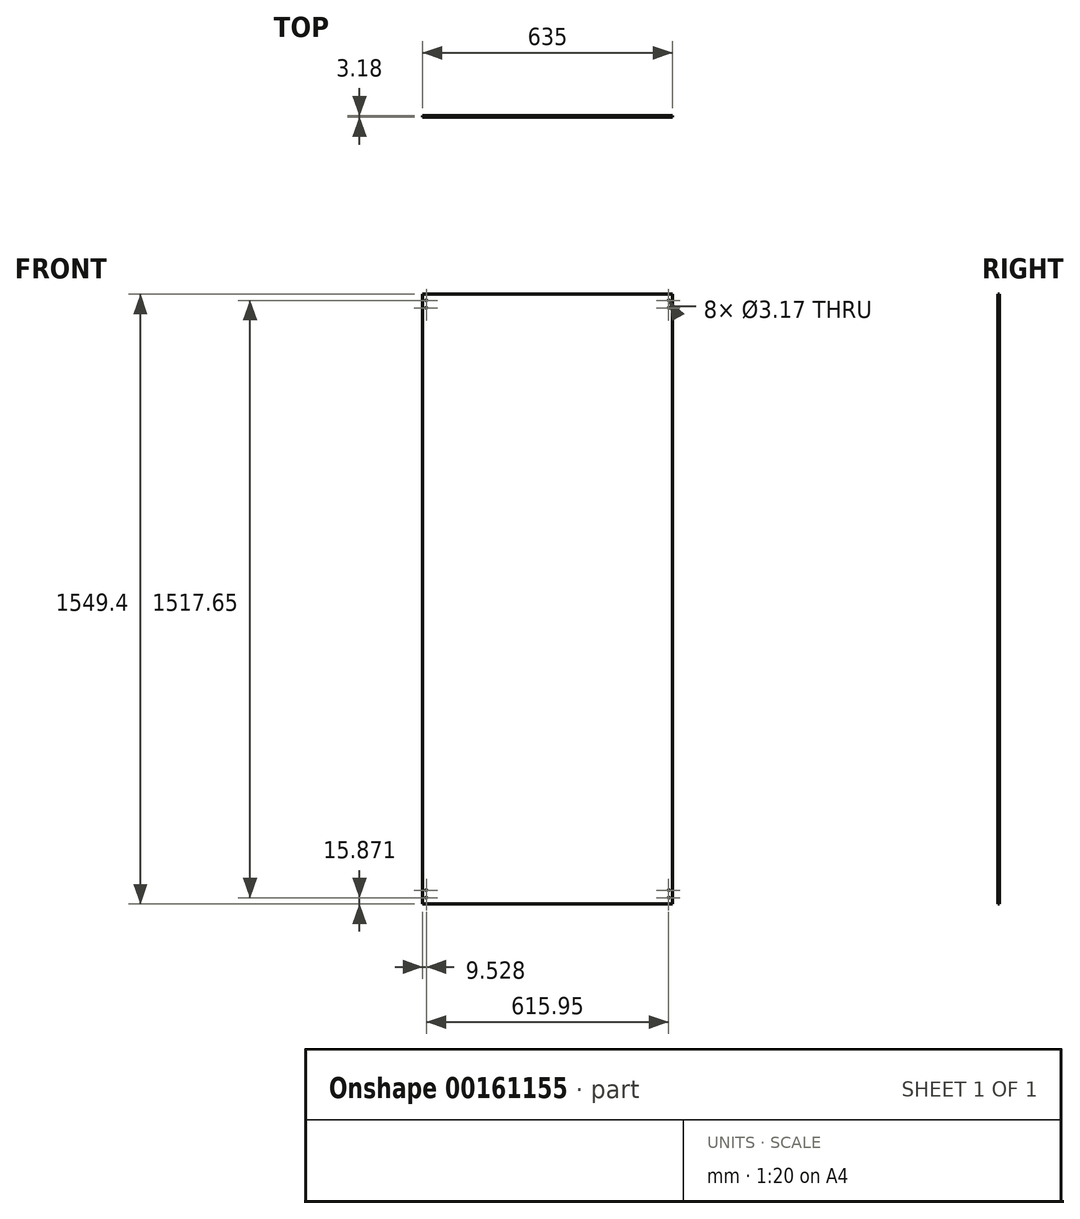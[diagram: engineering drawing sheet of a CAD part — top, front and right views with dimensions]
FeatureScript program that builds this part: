
annotation { "Feature Type Name" : "Feature", "Feature Type Description" : "" }
export const myFeature = defineFeature(function(context is Context, id is Id, definition is map)
    precondition{}
    {
        {
            var Q0;
            Q0=qCreatedBy(makeId("Front.planeOp"),FACE);
            var sketch = newSketch(context, id + "F0", { "sketchPlane" : qUnion([Q0])});
            skLineSegment(sketch, "E0.bottom", {"start": v(-379.1, 732.72) * mm, "end": v(255.9, 732.72) * mm});
            skLineSegment(sketch, "E0.left", {"start": v(-379.1, 732.72) * mm, "end": v(-379.1, -816.68) * mm});
            skLineSegment(sketch, "E0.right", {"start": v(255.9, 732.72) * mm, "end": v(255.9, -816.68) * mm});
            skLineSegment(sketch, "E1", {"start": v(255.9, -816.68) * mm, "end": v(-379.1, -816.68) * mm});
            skCircle(sketch, "E2", {"center": v(-369.57, -800.8) * mm, "radius": 1.59 * mm});
            skCircle(sketch, "E3", {"center": v(-369.57, -781.76) * mm, "radius": 1.59 * mm});
            skCircle(sketch, "E4", {"center": v(246.38, -800.8) * mm, "radius": 1.59 * mm});
            skCircle(sketch, "E5", {"center": v(246.38, -781.76) * mm, "radius": 1.59 * mm});
            skCircle(sketch, "E6", {"center": v(246.38, 716.84) * mm, "radius": 1.59 * mm});
            skCircle(sketch, "E7", {"center": v(246.38, 697.8) * mm, "radius": 1.59 * mm});
            skCircle(sketch, "E8", {"center": v(-369.57, 716.84) * mm, "radius": 1.59 * mm});
            skCircle(sketch, "E9", {"center": v(-369.57, 697.8) * mm, "radius": 1.59 * mm});
            skSolve(sketch);
        }
        {
            var Q0;
            Q0=makeQuery(id+"F0.imprint","IMPRINT",FACE,{"disambiguationData":[TD([[makeQuery(id+"F0.imprint","IMPRINT",EDGE,{"derivedFrom":sQuery(id+"F0.wireOp",EDGE,"E0.bottom")}),-1.0]])]});
            var Q1;
            Q1=sQuery(id+"F0.wireOp",EDGE,"E0.right");
            var Q2;
            Q2=sQuery(id+"F0.wireOp",EDGE,"E1");
            var Q3;
            Q3=sQuery(id+"F0.wireOp",EDGE,"E0.bottom");
            var Q4;
            Q4=sQuery(id+"F0.wireOp",EDGE,"E0.left");
            extrude(context, id + "F1", {"entities" : qUnion([Q0]), "surfaceEntities" : qUnion([Q1, Q2, Q3, Q4]), "depth" : 3.17 * mm});
        }
    });
